# Revit family: Urinal-Floor_Mount-KOHLER-MODERN_LIFE-K-21840T-1
name_source: partatom
category: Plumbing Fixtures
revit_build: Autodesk Revit 2017 (Build: 20160225_1515(x64)
units: mm (PartAtom-declared; Revit-internal decimal feet)

## family parameters
Cut with Voids When Loaded = No
Host = Face
OmniClass Number = 23.31.21.00
Part Type = Normal
Room Calculation Point = No
Round Connector Dimension = Use Diameter
Shared = No

## types (1)
- 0- White
    ADA Compliant = No
    Assembly Code = D2010200
    CW Connection = Yes
    Cold Water Inlet = Cold Water Inlet
    Date Modified = 04/07/2021
    Default Elevation = 0"
    Description = MODERN LIFE FS URINAL 1/3L, REAR
    Finish = Kohler-Vitreous_China-0-White
    Flow Rate = 0 GPM
    Flush Rate- GPF = 0 GPF
    Flush Rate- LPF = 0 LPF
    HW Connection = No
    Height = 39 7/16"
    Hot Water Inlet = Hot Water Inlet
    Internal Lip Height = 13"
    Length = 16"
    Manufacturer = KOHLER Co.
    Master Format 2014 = 22 41 13.16
    Master Format 2014 Name = Residential Urinals
    Material = Vitreous China
    Model = K-21840T-ER-0
    Pressure = 0.00 psi
    Product Name = MODERN LIFE
    Rough-In = 6 3/16"
    Type = 1
    URL = http://www.kohler.com.cn
    Vent Connection = No
    Waste Connection = Yes
    Waste Water Outlet = Waste Water Outlet
    WaterSense Certified = No
    Width = 12 1/4"

## geometry (parser evidence)
native form markers: Sweep x6
no freeform markers — native parametric forms only
